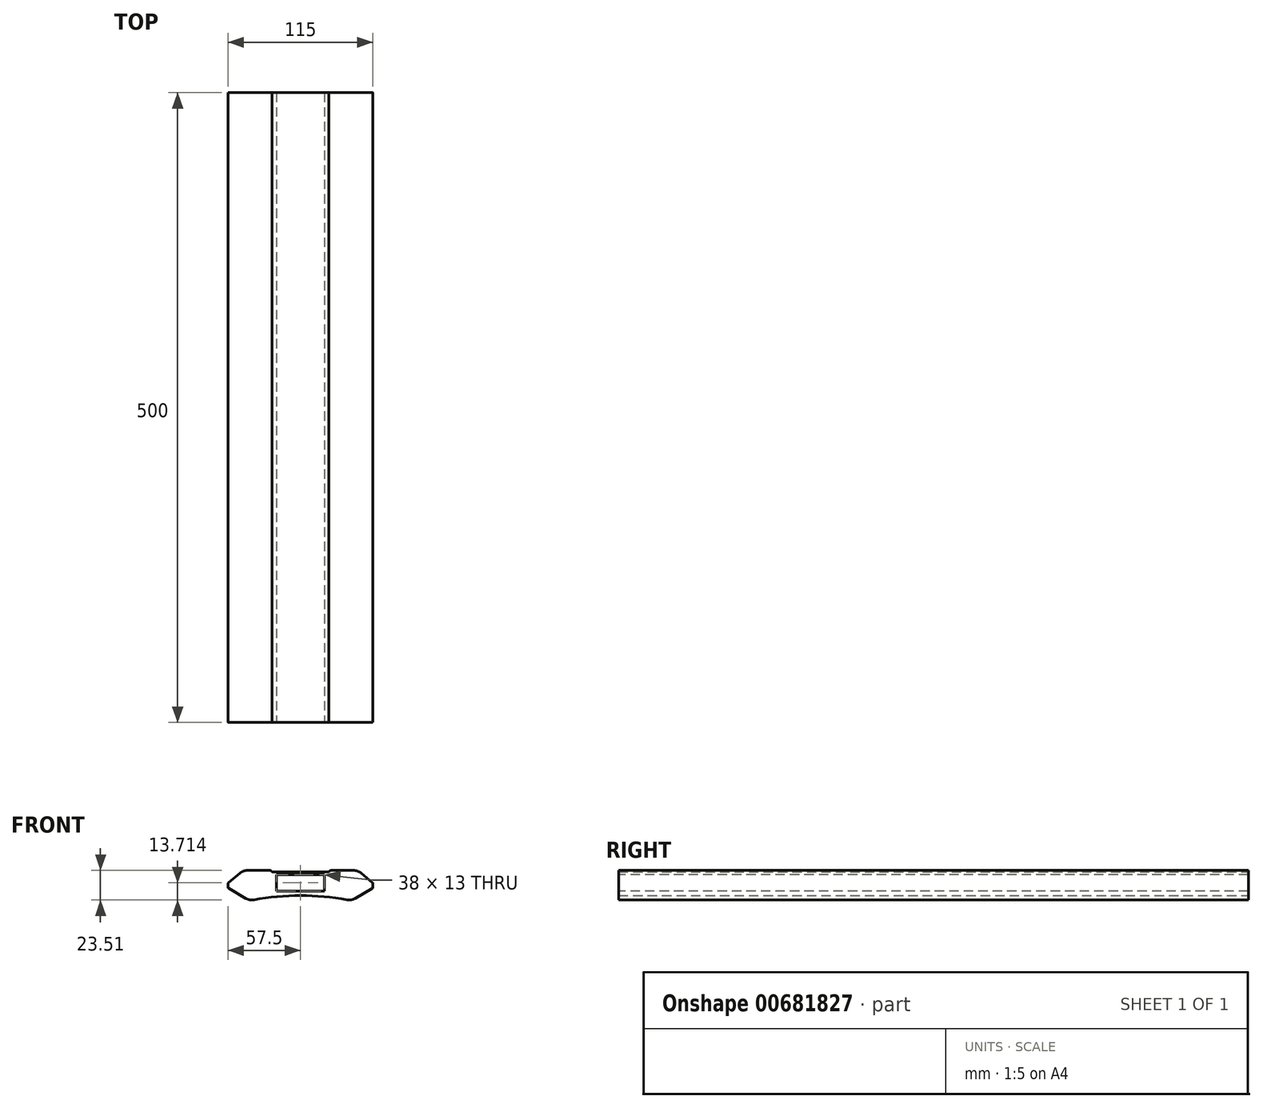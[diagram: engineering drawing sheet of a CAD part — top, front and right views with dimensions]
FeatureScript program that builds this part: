
annotation { "Feature Type Name" : "Feature", "Feature Type Description" : "" }
export const myFeature = defineFeature(function(context is Context, id is Id, definition is map)
    precondition{}
    {
        {
            var Q0;
            Q0=qCreatedBy(makeId("Front.planeOp"),FACE);
            var sketch = newSketch(context, id + "F0", { "sketchPlane" : qUnion([Q0])});
            skLineSegment(sketch, "E0", {"start": v(0, 0) * mm, "end": v(0, 17.89) * mm});
            skLineSegment(sketch, "E1", {"start": v(0, 16.4) * mm, "end": v(22.5, 16.4) * mm});
            skLineSegment(sketch, "E2", {"start": v(22.5, 16.4) * mm, "end": v(22.5, 17.7) * mm});
            skLineSegment(sketch, "E3", {"start": v(22.5, 17.7) * mm, "end": v(45.58, 17.7) * mm});
            skLineSegment(sketch, "E4", {"start": v(45.58, 17.7) * mm, "end": v(57.5, 7.7) * mm});
            skLineSegment(sketch, "E5", {"start": v(57.5, 7.7) * mm, "end": v(57.5, 3.7) * mm});
            skLineSegment(sketch, "E6", {"start": v(57.5, 3.7) * mm, "end": v(40.18, -6.3) * mm});
            skLineSegment(sketch, "E7.MirrorCS", {"start": v(0, 16.4) * mm, "end": v(-22.5, 16.4) * mm});
            skLineSegment(sketch, "E8.MirrorCS", {"start": v(-22.5, 16.4) * mm, "end": v(-22.5, 17.7) * mm});
            skLineSegment(sketch, "E9.MirrorCS", {"start": v(-22.5, 17.7) * mm, "end": v(-45.58, 17.7) * mm});
            skLineSegment(sketch, "E10.MirrorCS", {"start": v(-45.58, 17.7) * mm, "end": v(-57.5, 7.7) * mm});
            skLineSegment(sketch, "E11.MirrorCS", {"start": v(-57.5, 7.7) * mm, "end": v(-57.5, 3.7) * mm});
            skLineSegment(sketch, "E12.MirrorCS", {"start": v(-57.5, 3.7) * mm, "end": v(-40.18, -6.3) * mm});
            skArc(sketch, "E13", {"start": v(40.18, -6.3) * mm, "mid": v(0, -2.22) * mm, "end": v(-40.18, -6.3) * mm});
            skSolve(sketch);
        }
        {
            var Q0;
            Q0 = qSketchRegion(id + "F0", true);
            extrude(context, id + "F1", {"entities" : qUnion([Q0]), "endBound" : BoundingType.SYMMETRIC, "depth" : 500 * mm, "offsetDistance" : 25 * mm});
        }
        {
            var Q0;
            Q0=qCreatedBy(makeId("Front.planeOp"),FACE);
            var sketch = newSketch(context, id + "F2", { "sketchPlane" : qUnion([Q0])});
            skLineSegment(sketch, "E14.bottom", {"start": v(-19, 14.4) * mm, "end": v(19, 14.4) * mm});
            skLineSegment(sketch, "E14.top", {"start": v(-19, 1.4) * mm, "end": v(19, 1.4) * mm});
            skLineSegment(sketch, "E14.left", {"start": v(-19, 14.4) * mm, "end": v(-19, 1.4) * mm});
            skLineSegment(sketch, "E14.right", {"start": v(19, 14.4) * mm, "end": v(19, 1.4) * mm});
            skPoint(sketch, "E14.middle", {"position": v(0, 7.9) * mm});
            skSolve(sketch);
        }
        {
            var Q0;
            Q0 = qSketchRegion(id + "F2", true);
            extrude(context, id + "F3", {"entities" : qUnion([Q0]), "operationType" : NewBodyOperationType.REMOVE, "endBound" : BoundingType.SYMMETRIC, "oppositeDirection" : true, "depth" : 500 * mm, "offsetDistance" : 25 * mm});
        }
        {
            var Q0;
            Q0=makeQuery(id+"F1.opExtrude","SWEPT_EDGE",EDGE,{"disambiguationData":[OSD([sQuery(id+"F0.wireOp",EDGE,"E8.MirrorCS"),sQuery(id+"F0.wireOp",EDGE,"E9.MirrorCS")])]});
            var Q1;
            Q1=makeQuery(id+"F1.opExtrude","SWEPT_EDGE",EDGE,{"disambiguationData":[OSD([sQuery(id+"F0.wireOp",EDGE,"E2"),sQuery(id+"F0.wireOp",EDGE,"E3")])]});
            fillet(context, id + "F4", {"entities" : qUnion([Q0, Q1]), "radius" : 2 * mm, "tangentPropagation" : true, "allowEdgeOverflow" : false});
        }
        {
            var Q0;
            Q0=makeQuery(id+"F1.opExtrude","SWEPT_EDGE",EDGE,{"disambiguationData":[OSD([sQuery(id+"F0.wireOp",EDGE,"E3"),sQuery(id+"F0.wireOp",EDGE,"E4")])]});
            var Q1;
            Q1=makeQuery(id+"F1.opExtrude","SWEPT_EDGE",EDGE,{"disambiguationData":[OSD([sQuery(id+"F0.wireOp",EDGE,"E6"),sQuery(id+"F0.wireOp",EDGE,"E13")])]});
            var Q2;
            Q2=makeQuery(id+"F1.opExtrude","SWEPT_EDGE",EDGE,{"disambiguationData":[OSD([sQuery(id+"F0.wireOp",EDGE,"E12.MirrorCS"),sQuery(id+"F0.wireOp",EDGE,"E13")])]});
            var Q3;
            Q3=makeQuery(id+"F1.opExtrude","SWEPT_EDGE",EDGE,{"disambiguationData":[OSD([sQuery(id+"F0.wireOp",EDGE,"E9.MirrorCS"),sQuery(id+"F0.wireOp",EDGE,"E10.MirrorCS")])]});
            fillet(context, id + "F5", {"entities" : qUnion([Q0, Q1, Q2, Q3]), "radius" : 9 * mm, "tangentPropagation" : true, "allowEdgeOverflow" : false});
        }
        {
            var Q0;
            Q0=makeQuery(id+"F1.opExtrude","SWEPT_EDGE",EDGE,{"disambiguationData":[OSD([sQuery(id+"F0.wireOp",EDGE,"E5"),sQuery(id+"F0.wireOp",EDGE,"E6")])]});
            var Q1;
            Q1=makeQuery(id+"F1.opExtrude","SWEPT_EDGE",EDGE,{"disambiguationData":[OSD([sQuery(id+"F0.wireOp",EDGE,"E4"),sQuery(id+"F0.wireOp",EDGE,"E5")])]});
            var Q2;
            Q2=makeQuery(id+"F1.opExtrude","SWEPT_EDGE",EDGE,{"disambiguationData":[OSD([sQuery(id+"F0.wireOp",EDGE,"E10.MirrorCS"),sQuery(id+"F0.wireOp",EDGE,"E11.MirrorCS")])]});
            var Q3;
            Q3=makeQuery(id+"F1.opExtrude","SWEPT_EDGE",EDGE,{"disambiguationData":[OSD([sQuery(id+"F0.wireOp",EDGE,"E11.MirrorCS"),sQuery(id+"F0.wireOp",EDGE,"E12.MirrorCS")])]});
            fillet(context, id + "F6", {"entities" : qUnion([Q0, Q1, Q2, Q3]), "radius" : 1 * mm, "tangentPropagation" : true, "allowEdgeOverflow" : false});
        }
    });
